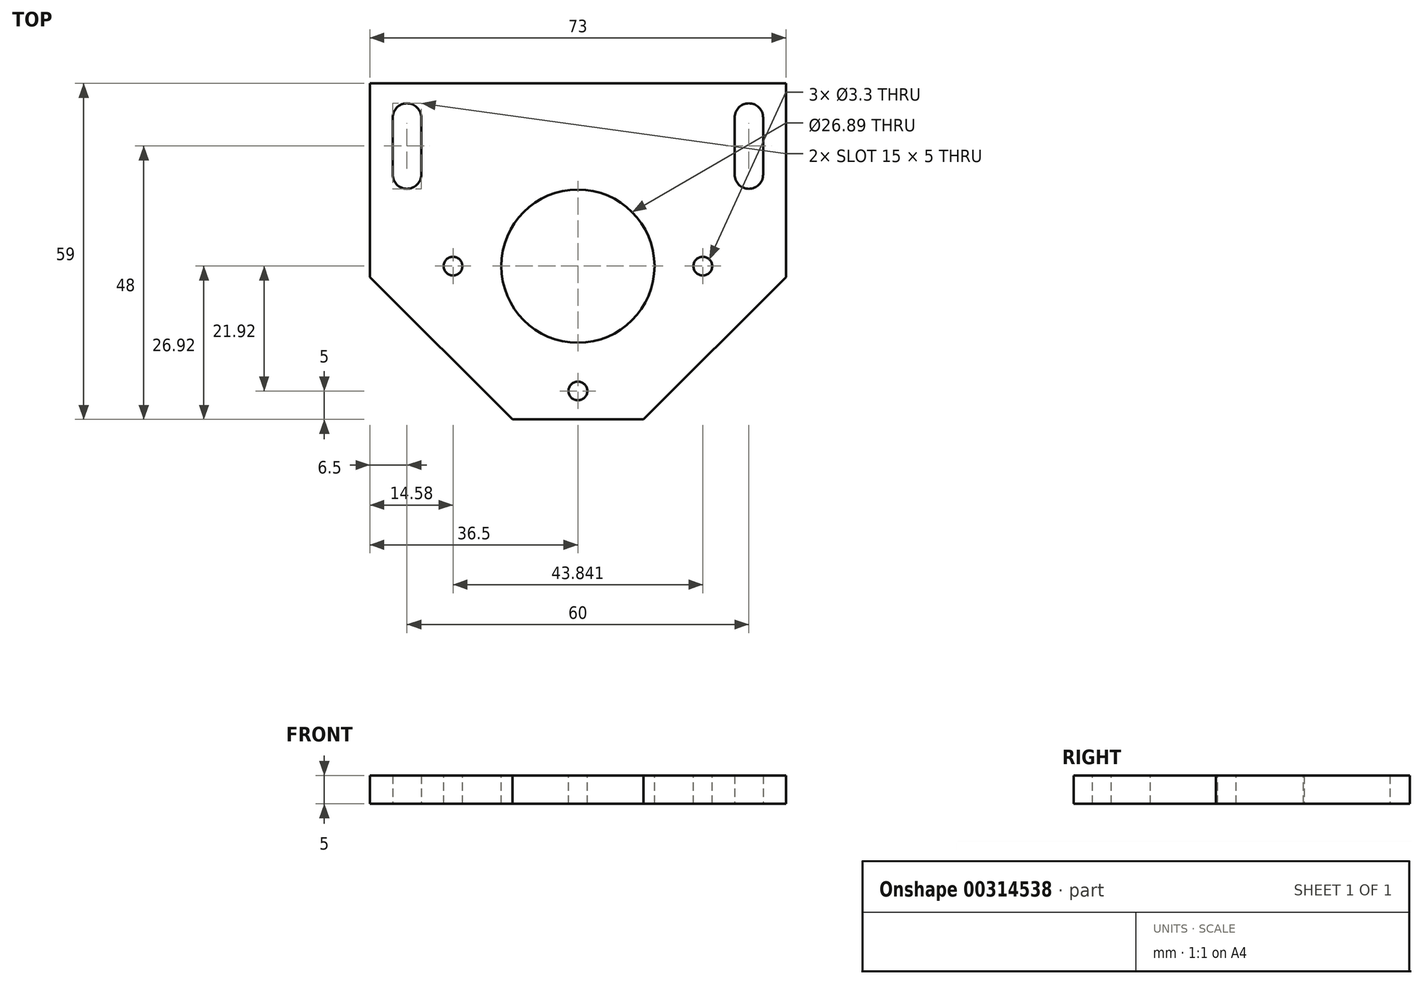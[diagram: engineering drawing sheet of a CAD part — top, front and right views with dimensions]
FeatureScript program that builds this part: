
annotation { "Feature Type Name" : "Feature", "Feature Type Description" : "" }
export const myFeature = defineFeature(function(context is Context, id is Id, definition is map)
    precondition{}
    {
        {
            var Q0;
            Q0=qCreatedBy(makeId("Top.planeOp"),FACE);
            var sketch = newSketch(context, id + "F0", { "sketchPlane" : qUnion([Q0])});
            skLineSegment(sketch, "E0.bottom", {"start": v(-36.5, -29.5) * mm, "end": v(36.5, -29.5) * mm});
            skLineSegment(sketch, "E0.top", {"start": v(-36.5, 29.5) * mm, "end": v(36.5, 29.5) * mm});
            skLineSegment(sketch, "E0.left", {"start": v(-36.5, -29.5) * mm, "end": v(-36.5, 29.5) * mm});
            skLineSegment(sketch, "E0.right", {"start": v(36.5, -29.5) * mm, "end": v(36.5, 29.5) * mm});
            skPoint(sketch, "E0.middle", {"position": v(0, 0) * mm});
            skLineSegment(sketch, "E1", {"start": v(-30, 23.5) * mm, "end": v(-30, 13.5) * mm});
            skLineSegment(sketch, "E2.1.0.0", {"start": v(30, 23.5) * mm, "end": v(30, 13.5) * mm});
            skLineSegment(sketch, "E2.direction1", {"start": v(-30, 13.5) * mm, "end": v(30, 13.5) * mm, "construction": true});
            skArc(sketch, "E3.0.startCap", {"start": v(-32.5, 23.5) * mm, "mid": v(-30, 26) * mm, "end": v(-27.5, 23.5) * mm});
            skArc(sketch, "E3.0.endCap", {"start": v(-27.5, 13.5) * mm, "mid": v(-30, 11) * mm, "end": v(-32.5, 13.5) * mm});
            skLineSegment(sketch, "E3.0.left", {"start": v(-27.5, 23.5) * mm, "end": v(-27.5, 13.5) * mm});
            skLineSegment(sketch, "E3.0.right", {"start": v(-32.5, 23.5) * mm, "end": v(-32.5, 13.5) * mm});
            skArc(sketch, "E3.1.startCap", {"start": v(27.5, 23.5) * mm, "mid": v(30, 26) * mm, "end": v(32.5, 23.5) * mm});
            skArc(sketch, "E3.1.endCap", {"start": v(32.5, 13.5) * mm, "mid": v(30, 11) * mm, "end": v(27.5, 13.5) * mm});
            skLineSegment(sketch, "E3.1.left", {"start": v(32.5, 23.5) * mm, "end": v(32.5, 13.5) * mm});
            skLineSegment(sketch, "E3.1.right", {"start": v(27.5, 23.5) * mm, "end": v(27.5, 13.5) * mm});
            skSolve(sketch);
        }
        {
            var Q0;
            Q0 = qSketchRegion(id + "F0", true);
            extrude(context, id + "F1", {"entities" : qUnion([Q0]), "depth" : 5 * mm});
        }
        {
            var Q0;
            Q0=makeQuery(id+"F1.opExtrude","SWEPT_EDGE",EDGE,{"disambiguationData":[OSD([sQuery(id+"F0.wireOp",EDGE,"E0.bottom"),sQuery(id+"F0.wireOp",EDGE,"E0.left")])]});
            var Q1;
            Q1=makeQuery(id+"F1.opExtrude","SWEPT_EDGE",EDGE,{"disambiguationData":[OSD([sQuery(id+"F0.wireOp",EDGE,"E0.bottom"),sQuery(id+"F0.wireOp",EDGE,"E0.right")])]});
            chamfer(context, id + "F2", {"entities" : qUnion([Q0, Q1]), "width" : 25 * mm, "tangentPropagation" : true});
        }
        {
            var Q0;
            Q0=makeQuery(id+"F1.opExtrude","CAP_FACE",FACE,{"disambiguationData":[OSD([sQuery(id+"F0.wireOp",EDGE,"E0.bottom"),sQuery(id+"F0.wireOp",EDGE,"E0.top"),sQuery(id+"F0.wireOp",EDGE,"E0.left"),sQuery(id+"F0.wireOp",EDGE,"E0.right"),sQuery(id+"F0.wireOp",EDGE,"E3.0.startCap"),sQuery(id+"F0.wireOp",EDGE,"E3.0.endCap"),sQuery(id+"F0.wireOp",EDGE,"E3.0.left"),sQuery(id+"F0.wireOp",EDGE,"E3.0.right"),sQuery(id+"F0.wireOp",EDGE,"E3.1.startCap"),sQuery(id+"F0.wireOp",EDGE,"E3.1.endCap"),sQuery(id+"F0.wireOp",EDGE,"E3.1.left"),sQuery(id+"F0.wireOp",EDGE,"E3.1.right")])],"isStart":false});
            var sketch = newSketch(context, id + "F3", { "sketchPlane" : qUnion([Q0])});
            skPoint(sketch, "E4", {"position": v(0, -24.5) * mm});
            skLineSegment(sketch, "E5", {"start": v(0, -24.5) * mm, "end": v(-21.92, -2.58) * mm, "construction": true});
            skLineSegment(sketch, "E6", {"start": v(0, -24.5) * mm, "end": v(-61.13, -24.5) * mm, "construction": true});
            skLineSegment(sketch, "E7.MirrorCS", {"start": v(0, -24.5) * mm, "end": v(21.92, -2.58) * mm, "construction": true});
            skPoint(sketch, "E8", {"position": v(-21.92, -2.58) * mm});
            skPoint(sketch, "E9", {"position": v(21.92, -2.58) * mm});
            skCircle(sketch, "E10", {"center": v(0, -2.58) * mm, "radius": 13.45 * mm});
            skSolve(sketch);
        }
        {
            var Q0;
            Q0=sQuery(id+"F3.wireOp",VERTEX,"E8");
            var Q1;
            Q1=sQuery(id+"F3.wireOp",VERTEX,"E4");
            var Q2;
            Q2=sQuery(id+"F3.wireOp",VERTEX,"E9");
            var Q3;
            Q3=makeQuery(id+"F1.opExtrude","SWEPT_BODY",BODY,{"disambiguationData":[OSD([sQuery(id+"F0.wireOp",EDGE,"E0.bottom"),sQuery(id+"F0.wireOp",EDGE,"E0.top"),sQuery(id+"F0.wireOp",EDGE,"E0.left"),sQuery(id+"F0.wireOp",EDGE,"E0.right"),sQuery(id+"F0.wireOp",EDGE,"E3.0.startCap"),sQuery(id+"F0.wireOp",EDGE,"E3.0.endCap"),sQuery(id+"F0.wireOp",EDGE,"E3.0.left"),sQuery(id+"F0.wireOp",EDGE,"E3.0.right"),sQuery(id+"F0.wireOp",EDGE,"E3.1.startCap"),sQuery(id+"F0.wireOp",EDGE,"E3.1.endCap"),sQuery(id+"F0.wireOp",EDGE,"E3.1.left"),sQuery(id+"F0.wireOp",EDGE,"E3.1.right")])]});
            hole(context, id + "F4", {"style" : HoleStyle.SIMPLE, "endStyle" : HoleEndStyle.BLIND, "standardTappedOrClearance" : lookupTablePath({ "standard" : "ISO", "fit" : "Normal", "size" : "M3", "type" : "Clearance" }), "standardBlindInLast" : lookupTablePath({ "fit" : "Standard", "standard" : "ISO", "size" : "M3", "type" : "Clearance" }), "holeDiameter" : 3.3 * mm, "holeDepth" : 13.8 * mm, "tappedDepth" : 12 * mm, "tapClearance" : 3, "locations" : qUnion([Q0, Q1, Q2]), "scope" : qUnion([Q3])});
        }
        {
            var Q0;
            Q0 = qSketchRegion(id + "F3", true);
            extrude(context, id + "F5", {"entities" : qUnion([Q0]), "operationType" : NewBodyOperationType.REMOVE, "endBound" : BoundingType.UP_TO_NEXT, "oppositeDirection" : true, "depth" : 25 * mm});
        }
    });
